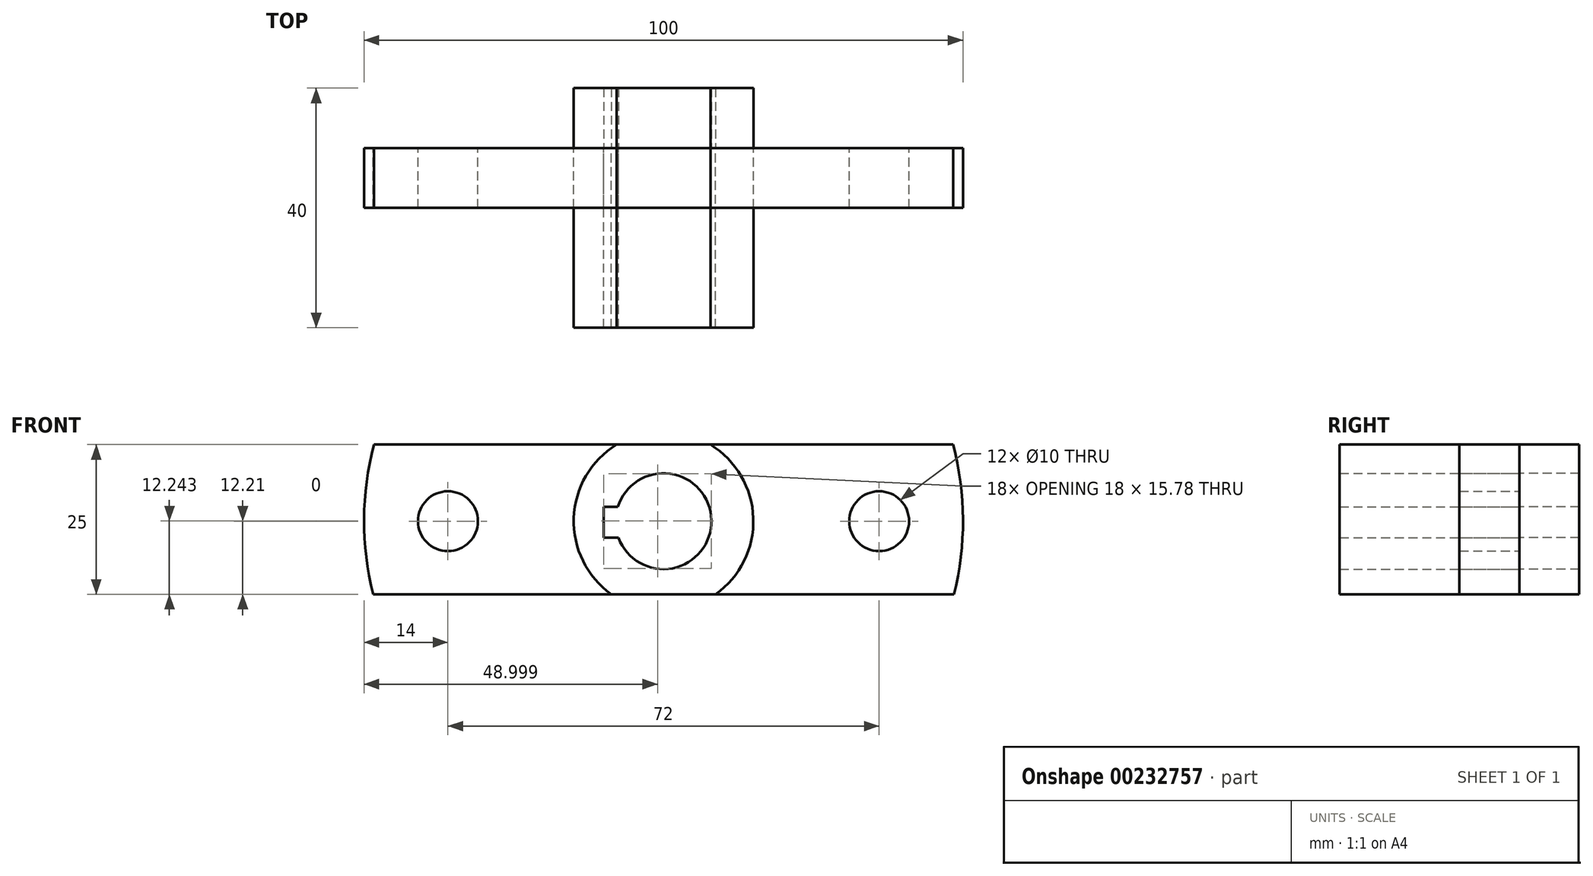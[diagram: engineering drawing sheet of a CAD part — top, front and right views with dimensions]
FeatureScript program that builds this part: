
annotation { "Feature Type Name" : "Feature", "Feature Type Description" : "" }
export const myFeature = defineFeature(function(context is Context, id is Id, definition is map)
    precondition{}
    {
        {
            var Q0;
            Q0=qCreatedBy(makeId("Front.planeOp"),FACE);
            var sketch = newSketch(context, id + "F0", { "sketchPlane" : qUnion([Q0])});
            skArc(sketch, "E0", {"start": v(-7.51, -2.76) * mm, "mid": v(8, 0.2) * mm, "end": v(-7.64, 2.37) * mm});
            skArc(sketch, "E1", {"start": v(-7.84, 12.79) * mm, "mid": v(-15, 0.52) * mm, "end": v(-8.7, -12.21) * mm});
            skCircle(sketch, "E2", {"center": v(-36, 0) * mm, "radius": 5 * mm});
            skCircle(sketch, "E3", {"center": v(36, 0) * mm, "radius": 5 * mm});
            skLineSegment(sketch, "E4.bottom", {"start": v(-48.34, 12.79) * mm, "end": v(48.34, 12.79) * mm});
            skLineSegment(sketch, "E4.top", {"start": v(-48.49, -12.21) * mm, "end": v(48.49, -12.21) * mm});
            skArc(sketch, "E5", {"start": v(-48.34, 12.79) * mm, "mid": v(-50, 0.3) * mm, "end": v(-48.49, -12.21) * mm});
            skLineSegment(sketch, "E6", {"start": v(-10, 2.37) * mm, "end": v(-10, -2.76) * mm});
            skLineSegment(sketch, "E7", {"start": v(-10, 2.37) * mm, "end": v(-7.64, 2.37) * mm});
            skLineSegment(sketch, "E8", {"start": v(-10, -2.76) * mm, "end": v(-7.51, -2.76) * mm});
            skArc(sketch, "E9.trimOffspring", {"start": v(48.49, -12.21) * mm, "mid": v(50, 0.3) * mm, "end": v(48.34, 12.79) * mm});
            skArc(sketch, "E10.trimOffspring", {"start": v(8.7, -12.21) * mm, "mid": v(15, 0.52) * mm, "end": v(7.84, 12.79) * mm});
            skSolve(sketch);
        }
        {
            var Q0;
            Q0=makeQuery(id+"F0.imprint","IMPRINT",FACE,{"disambiguationData":[TD([[makeQuery(id+"F0.imprint","IMPRINT",EDGE,{"derivedFrom":sQuery(id+"F0.wireOp",EDGE,"E0")}),-1.0]])]});
            extrude(context, id + "F1", {"entities" : qUnion([Q0]), "depth" : 30 * mm});
        }
        {
            var Q0;
            Q0 = qSketchRegion(id + "F0", true);
            extrude(context, id + "F2", {"entities" : qUnion([Q0]), "depth" : 10 * mm});
        }
        {
            var Q0;
            Q0=makeQuery(id+"F1.opExtrude","CAP_FACE",FACE,{"disambiguationData":[OSD([sQuery(id+"F0.wireOp",EDGE,"E0"),sQuery(id+"F0.wireOp",EDGE,"E1"),sQuery(id+"F0.wireOp",EDGE,"E4.bottom"),sQuery(id+"F0.wireOp",EDGE,"E4.top"),sQuery(id+"F0.wireOp",EDGE,"E6"),sQuery(id+"F0.wireOp",EDGE,"E7"),sQuery(id+"F0.wireOp",EDGE,"E8"),sQuery(id+"F0.wireOp",EDGE,"E10.trimOffspring")])],"isStart":true});
            extrude(context, id + "F3", {"entities" : qUnion([Q0]), "depth" : 10 * mm});
        }
    });
